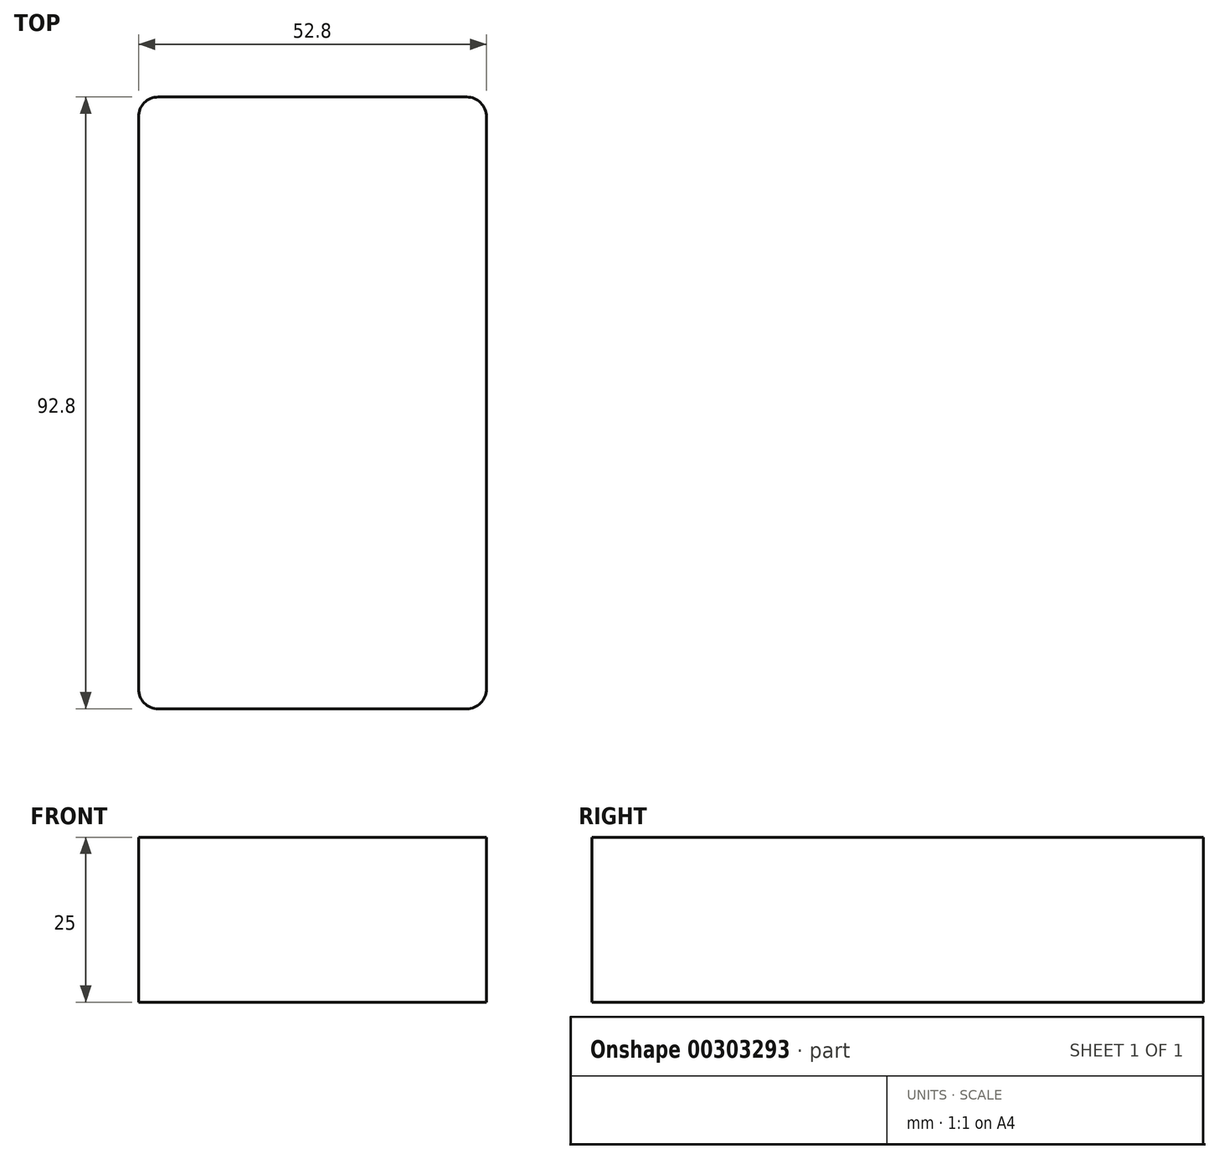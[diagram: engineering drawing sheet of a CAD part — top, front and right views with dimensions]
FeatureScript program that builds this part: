
annotation { "Feature Type Name" : "Feature", "Feature Type Description" : "" }
export const myFeature = defineFeature(function(context is Context, id is Id, definition is map)
    precondition{}
    {
        {
            var Q0;
            Q0=qCreatedBy(makeId("Top.planeOp"),FACE);
            var sketch = newSketch(context, id + "F0", { "sketchPlane" : qUnion([Q0])});
            skLineSegment(sketch, "E0", {"start": v(-38.25, 44.54) * mm, "end": v(15.75, 44.54) * mm});
            skLineSegment(sketch, "E1", {"start": v(18.75, 41.54) * mm, "end": v(18.75, -52.46) * mm});
            skLineSegment(sketch, "E2", {"start": v(15.75, -55.46) * mm, "end": v(-38.25, -55.46) * mm});
            skLineSegment(sketch, "E3", {"start": v(-41.25, -52.46) * mm, "end": v(-41.25, 41.54) * mm});
            skLineSegment(sketch, "E4", {"start": v(-11.25, -51.86) * mm, "end": v(12.15, -51.86) * mm});
            skLineSegment(sketch, "E5", {"start": v(-11.25, -51.86) * mm, "end": v(-34.65, -51.86) * mm});
            skLineSegment(sketch, "E6", {"start": v(-41.25, -55.46) * mm, "end": v(-37.65, -55.46) * mm});
            skLineSegment(sketch, "E7", {"start": v(-37.65, -48.86) * mm, "end": v(-37.65, 37.94) * mm});
            skLineSegment(sketch, "E8", {"start": v(-34.65, 40.94) * mm, "end": v(12.15, 40.94) * mm});
            skLineSegment(sketch, "E9", {"start": v(15.75, 44.54) * mm, "end": v(15.15, 44.54) * mm});
            skLineSegment(sketch, "E10", {"start": v(15.15, 37.94) * mm, "end": v(15.15, -48.86) * mm});
            skPoint(sketch, "E11.start.orphan", {"position": v(-11.25, -55.46) * mm});
            skArc(sketch, "E12.filletArc", {"start": v(-34.65, 40.94) * mm, "mid": v(-36.77, 40.06) * mm, "end": v(-37.65, 37.94) * mm});
            skPoint(sketch, "E13.visualSharp", {"position": v(15.15, 40.94) * mm});
            skArc(sketch, "E13.filletArc", {"start": v(15.15, 37.94) * mm, "mid": v(14.28, 40.06) * mm, "end": v(12.15, 40.94) * mm});
            skPoint(sketch, "E14.visualSharp", {"position": v(15.15, -51.86) * mm});
            skArc(sketch, "E14.filletArc", {"start": v(12.15, -51.86) * mm, "mid": v(14.28, -50.98) * mm, "end": v(15.15, -48.86) * mm});
            skPoint(sketch, "E15.visualSharp", {"position": v(-37.65, -51.86) * mm});
            skArc(sketch, "E15.filletArc", {"start": v(-37.65, -48.86) * mm, "mid": v(-36.77, -50.98) * mm, "end": v(-34.65, -51.86) * mm});
            skPoint(sketch, "E16.visualSharp", {"position": v(-41.25, -55.46) * mm});
            skArc(sketch, "E16.filletArc", {"start": v(-41.25, -52.46) * mm, "mid": v(-40.37, -54.58) * mm, "end": v(-38.25, -55.46) * mm});
            skPoint(sketch, "E17.visualSharp", {"position": v(18.75, -55.46) * mm});
            skArc(sketch, "E17.filletArc", {"start": v(15.75, -55.46) * mm, "mid": v(17.88, -54.58) * mm, "end": v(18.75, -52.46) * mm});
            skPoint(sketch, "E18.visualSharp", {"position": v(18.75, 44.54) * mm});
            skArc(sketch, "E18.filletArc", {"start": v(18.75, 41.54) * mm, "mid": v(17.88, 43.66) * mm, "end": v(15.75, 44.54) * mm});
            skPoint(sketch, "E19.visualSharp", {"position": v(-41.25, 44.54) * mm});
            skArc(sketch, "E19.filletArc", {"start": v(-38.25, 44.54) * mm, "mid": v(-40.37, 43.66) * mm, "end": v(-41.25, 41.54) * mm});
            skSolve(sketch);
        }
        {
            var Q0;
            Q0=makeQuery(id+"F0.imprint","IMPRINT",FACE,{"disambiguationData":[TD([[makeQuery(id+"F0.imprint","IMPRINT",EDGE,{"derivedFrom":sQuery(id+"F0.wireOp",EDGE,"E4")}),1.0]])]});
            extrude(context, id + "F1", {"entities" : qUnion([Q0]), "depth" : 25 * mm});
        }
    });
